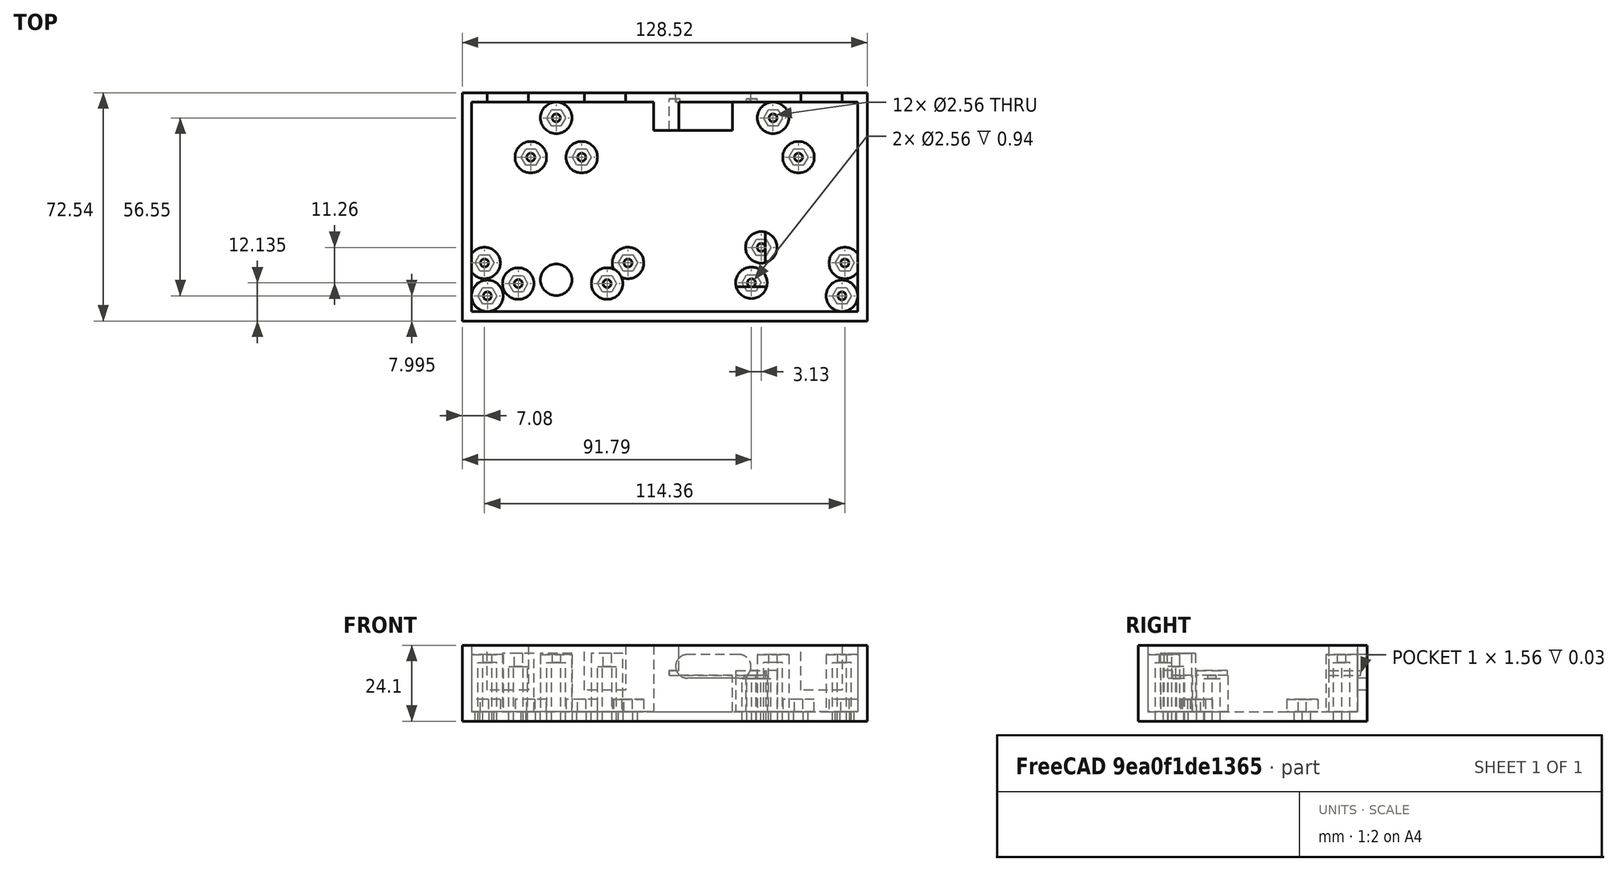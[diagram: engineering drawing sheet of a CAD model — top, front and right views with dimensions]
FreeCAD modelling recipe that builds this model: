
FCSTD DOCUMENT  (FreeCAD 1.0R38641 +678 (Git))
Label: box
License: All rights reserved
LicenseURL: https://en.wikipedia.org/wiki/All_rights_reserved
objects: Sketcher::SketchObject×19, PartDesign::Pocket×11, PartDesign::Pad×7, PartDesign::CoordinateSystem×1, PartDesign::Body×1
note: 94 computed .brp shape members not serialized (recipe doc carries the construction recipe); baked Part::Feature solids carry a one-line shape summary decoded from their .brp

FEATURE [Sketcher::SketchObject] Sketch
  ArcFitTolerance = 1e-06
  AttachmentSupport = -> [XY_Plane]
  FullyConstrained = true
  MakeInternals = false
  MapMode = 5
  sketch-geometry (4):
    g0: LineSegment StartX=-64.26 StartY=-36.275 StartZ=0 EndX=64.26 EndY=-36.275 EndZ=0
    g1: LineSegment StartX=64.26 StartY=-36.275 StartZ=0 EndX=64.26 EndY=36.275 EndZ=0
    g2: LineSegment StartX=64.26 StartY=36.275 StartZ=0 EndX=-64.26 EndY=36.275 EndZ=0
    g3: LineSegment StartX=-64.26 StartY=36.275 StartZ=0 EndX=-64.26 EndY=-36.275 EndZ=0
  constraints (12):
    c: Coincident(g0,g1)
    c: Coincident(g1,g2)
    c: Coincident(g2,g3)
    c: Coincident(g3,g0)
    c: Horizontal(g0)
    c: Horizontal(g2)
    c: Vertical(g1)
    c: Vertical(g3)
    c: DistanceX(g2,g2) = 128.52
    c: DistanceX(g-1,g1) = 64.26
    c: DistanceY(g3,g3) = 72.55
    c: DistanceY(g0,g-1) = 36.275
FEATURE [PartDesign::Pad] Pad
  Direction = (0,0,1)
  Length = 24.1
  Length2 = 10
  Profile = -> Sketch
  ReferenceAxis = -> Sketch [N_Axis]
  Refine = true
  Suppressed = false
  Type = 0
FEATURE [Sketcher::SketchObject] Sketch001
  ArcFitTolerance = 1e-06
  AttachmentSupport = -> [Pad]
  ExternalGeometry = -> [Pad]
  FullyConstrained = true
  MakeInternals = false
  MapMode = 5
  Placement = pos=(0,0,24.1) rot=(0,0,1;0rad)
  sketch-geometry (4):
    g0: LineSegment StartX=-61.26 StartY=-33.275 StartZ=0 EndX=61.26 EndY=-33.275 EndZ=0
    g1: LineSegment StartX=61.26 StartY=-33.275 StartZ=0 EndX=61.26 EndY=33.275 EndZ=0
    g2: LineSegment StartX=61.26 StartY=33.275 StartZ=0 EndX=-61.26 EndY=33.275 EndZ=0
    g3: LineSegment StartX=-61.26 StartY=33.275 StartZ=0 EndX=-61.26 EndY=-33.275 EndZ=0
  constraints (12):
    c: Coincident(g0,g1)
    c: Coincident(g1,g2)
    c: Coincident(g2,g3)
    c: Coincident(g3,g0)
    c: Horizontal(g0)
    c: Horizontal(g2)
    c: Vertical(g1)
    c: Vertical(g3)
    c: DistanceX(g-3,g2) = 3
    c: DistanceX(g0,g-4) = 3
    c: DistanceY(g-3,g0) = 3
    c: DistanceY(g1,g-4) = 3
FEATURE [PartDesign::Pocket] Pocket
  BaseFeature = -> Pad
  Direction = (0,0,-1)
  Length = 21.1
  Length2 = 5
  Profile = -> Sketch001
  ReferenceAxis = -> Sketch001 [N_Axis]
  Refine = true
  Suppressed = false
  Type = 0
FEATURE [Sketcher::SketchObject] Sketch002
  ArcFitTolerance = 1e-06
  AttachmentSupport = -> [Pocket]
  ExternalGeometry = -> [Pocket]
  FullyConstrained = true
  MakeInternals = false
  MapMode = 5
  Placement = pos=(0,0,3) rot=(0,0,1;0rad)
  sketch-geometry (6):
    g0: Circle CenterX=-42.48 CenterY=15.775 CenterZ=0 NormalX=0 NormalY=0 NormalZ=1 AngleXU=0 Radius=5
    g1: Circle CenterX=-57.18 CenterY=-17.825 CenterZ=0 NormalX=0 NormalY=0 NormalZ=1 AngleXU=0 Radius=5
    g2: Circle CenterX=-26.32 CenterY=15.775 CenterZ=0 NormalX=0 NormalY=0 NormalZ=1 AngleXU=0 Radius=5
    g3: Circle CenterX=-11.62 CenterY=-17.825 CenterZ=0 NormalX=0 NormalY=0 NormalZ=1 AngleXU=0 Radius=5
    g4: Circle CenterX=42.48 CenterY=15.775 CenterZ=0 NormalX=0 NormalY=0 NormalZ=1 AngleXU=0 Radius=5
    g5: Circle CenterX=57.18 CenterY=-17.825 CenterZ=0 NormalX=0 NormalY=0 NormalZ=1 AngleXU=0 Radius=5
  constraints (18):
    c: Radius(g0) = 5
    c: Equal(g0,g2)
    c: Equal(g2,g4)
    c: Equal(g4,g5)
    c: Equal(g5,g3)
    c: Equal(g3,g1)
    c: DistanceX(g-3,g0) = 21.78
    c: DistanceX(g-3,g2) = 37.94
    c: DistanceX(g4,g-4) = 21.78
    c: DistanceX(g5,g-4) = 7.08
    c: DistanceX(g-3,g1) = 7.08
    c: DistanceX(g-3,g3) = 52.64
    c: DistanceY(g0,g-3) = 20.5
    c: DistanceY(g-3,g1) = 18.45
    c: DistanceY(g0,g2) = 0
    c: DistanceY(g2,g4) = 0
    c: DistanceY(g1,g3) = 0
    c: DistanceY(g3,g5) = 0
FEATURE [PartDesign::Pad] Pad001
  BaseFeature = -> Pocket
  Direction = (0,0,1)
  Length = 3.9
  Length2 = 10
  Profile = -> Sketch002
  ReferenceAxis = -> Sketch002 [N_Axis]
  Refine = true
  Suppressed = false
  Type = 0
FEATURE [Sketcher::SketchObject] Sketch003
  ArcFitTolerance = 1e-06
  AttachmentSupport = -> [Pad001]
  ExternalGeometry = -> [Pad001]
  FullyConstrained = true
  MakeInternals = false
  MapMode = 5
  Placement = pos=(0,0,6.9) rot=(0,0,1;0rad)
  sketch-geometry (6):
    g0: Circle CenterX=-42.48 CenterY=15.775 CenterZ=0 NormalX=0 NormalY=0 NormalZ=1 AngleXU=0 Radius=1.28
    g1: Circle CenterX=-26.32 CenterY=15.775 CenterZ=0 NormalX=0 NormalY=0 NormalZ=1 AngleXU=0 Radius=1.28
    g2: Circle CenterX=42.48 CenterY=15.775 CenterZ=0 NormalX=0 NormalY=0 NormalZ=1 AngleXU=0 Radius=1.28
    g3: Circle CenterX=57.18 CenterY=-17.825 CenterZ=0 NormalX=0 NormalY=0 NormalZ=1 AngleXU=0 Radius=1.28
    g4: Circle CenterX=-11.62 CenterY=-17.825 CenterZ=0 NormalX=0 NormalY=0 NormalZ=1 AngleXU=0 Radius=1.28
    g5: Circle CenterX=-57.18 CenterY=-17.825 CenterZ=0 NormalX=0 NormalY=0 NormalZ=1 AngleXU=0 Radius=1.28
  constraints (12):
    c: Radius(g0) = 1.28
    c: Equal(g0,g1)
    c: Equal(g1,g2)
    c: Equal(g2,g3)
    c: Equal(g3,g4)
    c: Equal(g4,g5)
    c: Coincident(g0,g-3)
    c: Coincident(g1,g-4)
    c: Coincident(g2,g-5)
    c: Coincident(g3,g-6)
    c: Coincident(g4,g-7)
    c: Coincident(g5,g-8)
FEATURE [PartDesign::Pocket] Pocket001
  BaseFeature = -> Pad001
  Direction = (0,0,-1)
  Length = 3.9
  Length2 = 5
  Profile = -> Sketch003
  ReferenceAxis = -> Sketch003 [N_Axis]
  Refine = true
  Suppressed = false
  Type = 0
FEATURE [Sketcher::SketchObject] Sketch004
  ArcFitTolerance = 1e-06
  AttachmentSupport = -> [Pocket001]
  ExternalGeometry = -> [Pocket001]
  FullyConstrained = true
  MakeInternals = false
  MapMode = 5
  Placement = pos=(0,0,3) rot=(0,0,1;0rad)
  sketch-geometry (6):
    g0: LineSegment StartX=-3.54 StartY=24.275 StartZ=0 EndX=21.46 EndY=24.275 EndZ=0
    g1: LineSegment StartX=21.46 StartY=24.275 StartZ=0 EndX=21.46 EndY=34.275 EndZ=0
    g2: LineSegment StartX=21.46 StartY=34.275 StartZ=0 EndX=-3.54 EndY=34.275 EndZ=0
    g3: LineSegment StartX=-3.54 StartY=34.275 StartZ=0 EndX=-3.54 EndY=24.275 EndZ=0
    g4: Circle CenterX=27.53 CenterY=-24.135 CenterZ=0 NormalX=0 NormalY=0 NormalZ=1 AngleXU=0 Radius=5
    g5: Circle CenterX=30.66 CenterY=-12.875 CenterZ=0 NormalX=0 NormalY=0 NormalZ=1 AngleXU=0 Radius=5
  constraints (18):
    c: Coincident(g0,g1)
    c: Coincident(g1,g2)
    c: Coincident(g2,g3)
    c: Coincident(g3,g0)
    c: Horizontal(g0)
    c: Horizontal(g2)
    c: Vertical(g1)
    c: Vertical(g3)
    c: Radius(g5) = 5
    c: Equal(g5,g4)
    c: DistanceY(g3,g3) = 10
    c: DistanceX(g0,g0) = 25
    c: DistanceX(g1,g-3) = 42.8
    c: DistanceY(g1,g-3) = 2
    c: DistanceY(g-3,g5) = 23.4
    c: DistanceY(g-3,g4) = 12.14
    c: DistanceX(g5,g-3) = 33.6
    c: DistanceX(g4,g-3) = 36.73
FEATURE [PartDesign::Pad] Pad002
  BaseFeature = -> Pocket001
  Direction = (0,0,1)
  Length = 11.5
  Length2 = 10
  Profile = -> Sketch004
  ReferenceAxis = -> Sketch004 [N_Axis]
  Refine = true
  Suppressed = false
  Type = 0
FEATURE [Sketcher::SketchObject] Sketch005
  ArcFitTolerance = 1e-06
  AttachmentSupport = -> [Pad002]
  ExternalGeometry = -> [Pad002]
  FullyConstrained = true
  MakeInternals = false
  MapMode = 5
  Placement = pos=(0,0,14.5) rot=(0,0,1;0rad)
  sketch-geometry (2):
    g0: Circle CenterX=30.66 CenterY=-12.875 CenterZ=0 NormalX=0 NormalY=0 NormalZ=1 AngleXU=0 Radius=1.28
    g1: Circle CenterX=27.53 CenterY=-24.135 CenterZ=0 NormalX=0 NormalY=0 NormalZ=1 AngleXU=0 Radius=1.28
  constraints (4):
    c: Radius(g0) = 1.28
    c: Equal(g0,g1)
    c: Coincident(g0,g-3)
    c: Coincident(g1,g-4)
FEATURE [PartDesign::Pocket] Pocket002
  BaseFeature = -> Pad002
  Direction = (0,0,-1)
  Length = 3.94
  Length2 = 5
  Profile = -> Sketch005
  ReferenceAxis = -> Sketch005 [N_Axis]
  Refine = true
  Suppressed = false
  Type = 0
FEATURE [Sketcher::SketchObject] Sketch006
  ArcFitTolerance = 1e-06
  AttachmentSupport = -> [Pocket002]
  ExternalGeometry = -> [Pocket002]
  FullyConstrained = true
  MakeInternals = false
  MapMode = 5
  Placement = pos=(0,0,3) rot=(0,0,1;0rad)
  sketch-geometry (3):
    g0: Circle CenterX=-46.46 CenterY=-24.375 CenterZ=0 NormalX=0 NormalY=0 NormalZ=1 AngleXU=0 Radius=5
    g1: Circle CenterX=-18.26 CenterY=-24.375 CenterZ=0 NormalX=0 NormalY=0 NormalZ=1 AngleXU=0 Radius=5
    g2: Circle CenterX=-34.4 CenterY=-23.175 CenterZ=0 NormalX=0 NormalY=0 NormalZ=1 AngleXU=0 Radius=5
  constraints (9):
    c: Radius(g0) = 5
    c: Equal(g0,g2)
    c: Equal(g2,g1)
    c: DistanceX(g-3,g0) = 17.8
    c: DistanceX(g-3,g2) = 29.86
    c: DistanceX(g-3,g1) = 46
    c: DistanceY(g-3,g0) = 11.9
    c: DistanceY(g0,g1) = 0
    c: DistanceY(g-3,g2) = 13.1
FEATURE [PartDesign::Pad] Pad003
  BaseFeature = -> Pocket002
  Direction = (0,0,1)
  Length = 18.5
  Length2 = 10
  Profile = -> Sketch006
  ReferenceAxis = -> Sketch006 [N_Axis]
  Refine = true
  Suppressed = false
  Type = 0
FEATURE [Sketcher::SketchObject] Sketch007
  ArcFitTolerance = 1e-06
  AttachmentSupport = -> [Pad003]
  ExternalGeometry = -> [Pad003]
  FullyConstrained = true
  MakeInternals = false
  MapMode = 5
  Placement = pos=(0,0,21.5) rot=(0,0,1;0rad)
  sketch-geometry (2):
    g0: Circle CenterX=-46.46 CenterY=-24.375 CenterZ=0 NormalX=0 NormalY=0 NormalZ=1 AngleXU=0 Radius=1.28
    g1: Circle CenterX=-18.26 CenterY=-24.375 CenterZ=0 NormalX=0 NormalY=0 NormalZ=1 AngleXU=0 Radius=1.28
  constraints (4):
    c: Radius(g0) = 1.28
    c: Radius(g1) = 1.28
    c: Coincident(g0,g-4)
    c: Coincident(g1,g-3)
FEATURE [PartDesign::Pocket] Pocket003
  BaseFeature = -> Pad003
  Direction = (0,0,-1)
  Length = 4.1
  Length2 = 5
  Profile = -> Sketch007
  ReferenceAxis = -> Sketch007 [N_Axis]
  Refine = true
  Suppressed = false
  Type = 0
FEATURE [Sketcher::SketchObject] Sketch008
  ArcFitTolerance = 1e-06
  AttachmentSupport = -> [Pocket003]
  ExternalGeometry = -> [Pocket003]
  FullyConstrained = true
  MakeInternals = false
  MapMode = 5
  Placement = pos=(0,0,3) rot=(0,0,1;0rad)
  sketch-geometry (4):
    g0: Circle CenterX=-34.4 CenterY=28.275 CenterZ=0 NormalX=0 NormalY=0 NormalZ=1 AngleXU=0 Radius=5
    g1: Circle CenterX=34.4 CenterY=28.275 CenterZ=0 NormalX=0 NormalY=0 NormalZ=1 AngleXU=0 Radius=5
    g2: Circle CenterX=-56.26 CenterY=-28.275 CenterZ=0 NormalX=0 NormalY=0 NormalZ=1 AngleXU=0 Radius=5
    g3: Circle CenterX=56.26 CenterY=-28.275 CenterZ=0 NormalX=0 NormalY=0 NormalZ=1 AngleXU=0 Radius=5
  constraints (12):
    c: Radius(g0) = 5
    c: Equal(g1,g0)
    c: Equal(g1,g2)
    c: Equal(g2,g3)
    c: DistanceX(g-3,g0) = 29.86
    c: DistanceX(g1,g-4) = 29.86
    c: DistanceX(g-3,g2) = 8
    c: DistanceX(g3,g-4) = 8
    c: DistanceY(g0,g-3) = 8
    c: DistanceY(g1,g-4) = 8
    c: DistanceY(g-4,g3) = 8
    c: DistanceY(g-3,g2) = 8
FEATURE [PartDesign::Pad] Pad004
  BaseFeature = -> Pocket003
  Direction = (0,0,1)
  Length = 18.1
  Length2 = 10
  Profile = -> Sketch008
  ReferenceAxis = -> Sketch008 [N_Axis]
  Refine = true
  Suppressed = false
  Type = 0
FEATURE [Sketcher::SketchObject] Sketch009
  ArcFitTolerance = 1e-06
  AttachmentSupport = -> [Pad004]
  ExternalGeometry = -> [Pad004]
  FullyConstrained = true
  MakeInternals = false
  MapMode = 5
  Placement = pos=(0,0,21.1) rot=(0,0,1;0rad)
  sketch-geometry (4):
    g0: Circle CenterX=-34.4 CenterY=28.275 CenterZ=0 NormalX=0 NormalY=0 NormalZ=1 AngleXU=0 Radius=1.28
    g1: Circle CenterX=34.4 CenterY=28.275 CenterZ=0 NormalX=0 NormalY=0 NormalZ=1 AngleXU=0 Radius=1.28
    g2: Circle CenterX=56.26 CenterY=-28.275 CenterZ=0 NormalX=0 NormalY=0 NormalZ=1 AngleXU=0 Radius=1.28
    g3: Circle CenterX=-56.26 CenterY=-28.275 CenterZ=0 NormalX=0 NormalY=0 NormalZ=1 AngleXU=0 Radius=1.28
  constraints (8):
    c: Radius(g0) = 1.28
    c: Equal(g0,g1)
    c: Equal(g1,g2)
    c: Equal(g2,g3)
    c: Coincident(g0,g-3)
    c: Coincident(g1,g-4)
    c: Coincident(g2,g-5)
    c: Coincident(g3,g-6)
FEATURE [PartDesign::Pocket] Pocket004
  BaseFeature = -> Pad004
  Direction = (0,0,-1)
  Length = 2.5
  Length2 = 5
  Profile = -> Sketch009
  ReferenceAxis = -> Sketch009 [N_Axis]
  Refine = true
  Suppressed = false
  Type = 0
FEATURE [Sketcher::SketchObject] Sketch010
  ArcFitTolerance = 1e-06
  AttachmentSupport = -> [Pocket004]
  ExternalGeometry = -> [Pocket004]
  FullyConstrained = true
  MakeInternals = false
  MapMode = 5
  Placement = pos=(0,0,0) rot=(1,0,0;3.14159rad)
  sketch-geometry (42):
    g0: LineSegment StartX=-54.18 StartY=17.825 StartZ=0 EndX=-55.68 EndY=20.4231 EndZ=0
    g1: LineSegment StartX=-55.68 StartY=20.4231 StartZ=0 EndX=-58.68 EndY=20.4231 EndZ=0
    g2: LineSegment StartX=-58.68 StartY=20.4231 StartZ=0 EndX=-60.18 EndY=17.825 EndZ=0
    g3: LineSegment StartX=-60.18 StartY=17.825 StartZ=0 EndX=-58.68 EndY=15.2269 EndZ=0
    g4: LineSegment StartX=-58.68 StartY=15.2269 StartZ=0 EndX=-55.68 EndY=15.2269 EndZ=0
    g5: LineSegment StartX=-55.68 StartY=15.2269 StartZ=0 EndX=-54.18 EndY=17.825 EndZ=0
    g6: Circle [constr] CenterX=-57.18 CenterY=17.825 CenterZ=0 NormalX=0 NormalY=0 NormalZ=1 AngleXU=0 Radius=3
    g7: LineSegment StartX=-40.98 StartY=-18.3731 StartZ=0 EndX=-39.48 EndY=-15.775 EndZ=0
    g8: LineSegment StartX=-39.48 StartY=-15.775 StartZ=0 EndX=-40.98 EndY=-13.1769 EndZ=0
    g9: LineSegment StartX=-40.98 StartY=-13.1769 StartZ=0 EndX=-43.98 EndY=-13.1769 EndZ=0
    g10: LineSegment StartX=-43.98 StartY=-13.1769 StartZ=0 EndX=-45.48 EndY=-15.775 EndZ=0
    g11: LineSegment StartX=-45.48 StartY=-15.775 StartZ=0 EndX=-43.98 EndY=-18.3731 EndZ=0
    g12: LineSegment StartX=-43.98 StartY=-18.3731 StartZ=0 EndX=-40.98 EndY=-18.3731 EndZ=0
    g13: Circle [constr] CenterX=-42.48 CenterY=-15.775 CenterZ=0 NormalX=0 NormalY=0 NormalZ=1 AngleXU=0 Radius=3
    g14: LineSegment StartX=-23.32 StartY=-15.775 StartZ=0 EndX=-24.82 EndY=-13.1769 EndZ=0
    g15: LineSegment StartX=-24.82 StartY=-13.1769 StartZ=0 EndX=-27.82 EndY=-13.1769 EndZ=0
    g16: LineSegment StartX=-27.82 StartY=-13.1769 StartZ=0 EndX=-29.32 EndY=-15.775 EndZ=0
    g17: LineSegment StartX=-29.32 StartY=-15.775 StartZ=0 EndX=-27.82 EndY=-18.3731 EndZ=0
    g18: LineSegment StartX=-27.82 StartY=-18.3731 StartZ=0 EndX=-24.82 EndY=-18.3731 EndZ=0
    g19: LineSegment StartX=-24.82 StartY=-18.3731 StartZ=0 EndX=-23.32 EndY=-15.775 EndZ=0
    g20: Circle [constr] CenterX=-26.32 CenterY=-15.775 CenterZ=0 NormalX=0 NormalY=0 NormalZ=1 AngleXU=0 Radius=3
    g21: LineSegment StartX=-10.12 StartY=15.2269 StartZ=0 EndX=-8.62 EndY=17.825 EndZ=0
    g22: LineSegment StartX=-8.62 StartY=17.825 StartZ=0 EndX=-10.12 EndY=20.4231 EndZ=0
    g23: LineSegment StartX=-10.12 StartY=20.4231 StartZ=0 EndX=-13.12 EndY=20.4231 EndZ=0
    g24: LineSegment StartX=-13.12 StartY=20.4231 StartZ=0 EndX=-14.62 EndY=17.825 EndZ=0
    g25: LineSegment StartX=-14.62 StartY=17.825 StartZ=0 EndX=-13.12 EndY=15.2269 EndZ=0
    g26: LineSegment StartX=-13.12 StartY=15.2269 StartZ=0 EndX=-10.12 EndY=15.2269 EndZ=0
    g27: Circle [constr] CenterX=-11.62 CenterY=17.825 CenterZ=0 NormalX=0 NormalY=0 NormalZ=1 AngleXU=0 Radius=3
    g28: LineSegment StartX=58.68 StartY=15.2269 StartZ=0 EndX=60.18 EndY=17.825 EndZ=0
    g29: LineSegment StartX=60.18 StartY=17.825 StartZ=0 EndX=58.68 EndY=20.4231 EndZ=0
    g30: LineSegment StartX=58.68 StartY=20.4231 StartZ=0 EndX=55.68 EndY=20.4231 EndZ=0
    g31: LineSegment StartX=55.68 StartY=20.4231 StartZ=0 EndX=54.18 EndY=17.825 EndZ=0
    g32: LineSegment StartX=54.18 StartY=17.825 StartZ=0 EndX=55.68 EndY=15.2269 EndZ=0
    g33: LineSegment StartX=55.68 StartY=15.2269 StartZ=0 EndX=58.68 EndY=15.2269 EndZ=0
    g34: Circle [constr] CenterX=57.18 CenterY=17.825 CenterZ=0 NormalX=0 NormalY=0 NormalZ=1 AngleXU=0 Radius=3
    g35: LineSegment StartX=43.98 StartY=-18.3731 StartZ=0 EndX=45.48 EndY=-15.775 EndZ=0
    g36: LineSegment StartX=45.48 StartY=-15.775 StartZ=0 EndX=43.98 EndY=-13.1769 EndZ=0
    g37: LineSegment StartX=43.98 StartY=-13.1769 StartZ=0 EndX=40.98 EndY=-13.1769 EndZ=0
    g38: LineSegment StartX=40.98 StartY=-13.1769 StartZ=0 EndX=39.48 EndY=-15.775 EndZ=0
    g39: LineSegment StartX=39.48 StartY=-15.775 StartZ=0 EndX=40.98 EndY=-18.3731 EndZ=0
    g40: LineSegment StartX=40.98 StartY=-18.3731 StartZ=0 EndX=43.98 EndY=-18.3731 EndZ=0
    g41: Circle [constr] CenterX=42.48 CenterY=-15.775 CenterZ=0 NormalX=0 NormalY=0 NormalZ=1 AngleXU=0 Radius=3
  constraints (102):
    c: Coincident(g0,g1)
    c: Coincident(g1,g2)
    c: Coincident(g2,g3)
    c: Coincident(g3,g4)
    c: Coincident(g4,g5)
    c: Coincident(g5,g0)
    c: Equal(g0, g1-g5) x5
    c: PointOnObject(g0,g6)
    c: PointOnObject(g1,g6)
    c: PointOnObject(g2,g6)
    c: PointOnObject(g3,g6)
    c: PointOnObject(g4,g6)
    c: PointOnObject(g5,g6)
    c: Coincident(g7,g8)
    c: Coincident(g8,g9)
    c: Coincident(g9,g10)
    c: Coincident(g10,g11)
    c: Coincident(g11,g12)
    c: Coincident(g12,g7)
    c: Equal(g7, g8-g12) x5
    c: PointOnObject(g7,g13)
    c: PointOnObject(g8,g13)
    c: PointOnObject(g9,g13)
    c: PointOnObject(g10,g13)
    c: PointOnObject(g11,g13)
    c: PointOnObject(g12,g13)
    c: Coincident(g14,g15)
    c: Coincident(g15,g16)
    c: Coincident(g16,g17)
    c: Coincident(g17,g18)
    c: Coincident(g18,g19)
    c: Coincident(g19,g14)
    c: Equal(g14, g15-g19) x5
    c: PointOnObject(g14,g20)
    c: PointOnObject(g15,g20)
    c: PointOnObject(g16,g20)
    c: PointOnObject(g17,g20)
    c: PointOnObject(g18,g20)
    c: PointOnObject(g19,g20)
    c: Coincident(g21,g22)
    c: Coincident(g22,g23)
    c: Coincident(g23,g24)
    c: Coincident(g24,g25)
    c: Coincident(g25,g26)
    c: Coincident(g26,g21)
    c: Equal(g21, g22-g26) x5
    c: PointOnObject(g21,g27)
    c: PointOnObject(g22,g27)
    c: PointOnObject(g23,g27)
    c: PointOnObject(g24,g27)
    c: PointOnObject(g25,g27)
    c: PointOnObject(g26,g27)
    c: Coincident(g28,g29)
    c: Coincident(g29,g30)
    c: Coincident(g30,g31)
    c: Coincident(g31,g32)
    c: Coincident(g32,g33)
    c: Coincident(g33,g28)
    c: Equal(g28, g29-g33) x5
    c: PointOnObject(g28,g34)
    c: PointOnObject(g29,g34)
    c: PointOnObject(g30,g34)
    c: PointOnObject(g31,g34)
    c: PointOnObject(g32,g34)
    c: PointOnObject(g33,g34)
    c: Coincident(g35,g36)
    c: Coincident(g36,g37)
    c: Coincident(g37,g38)
    c: Coincident(g38,g39)
    c: Coincident(g39,g40)
    c: Coincident(g40,g35)
    c: Equal(g35, g36-g40) x5
    c: PointOnObject(g35,g41)
    c: PointOnObject(g36,g41)
    c: PointOnObject(g37,g41)
    c: PointOnObject(g38,g41)
    c: PointOnObject(g39,g41)
    c: PointOnObject(g40,g41)
    c: Radius(g6) = 3
    c: Horizontal(g1)
    c: Horizontal(g23)
    c: Horizontal(g30)
    c: Horizontal(g37)
    c: Horizontal(g15)
    c: Horizontal(g9)
    c: Equal(g6,g27)
    c: Equal(g27,g34)
    c: Equal(g34,g41)
    c: Equal(g41,g20)
    c: Equal(g20,g13)
    c: DistanceY(g6,g27) = 0
    c: DistanceY(g27,g34) = 0
    c: DistanceY(g41,g20) = 0
    c: DistanceY(g13,g20) = 0
    c: DistanceX(g-3,g6) = 7.08
    c: DistanceX(g34,g-4) = 7.08
    c: DistanceX(g-3,g13) = 21.78
    c: DistanceX(g41,g-4) = 21.78
    c: DistanceX(g-3,g20) = 37.94
    c: DistanceY(g-3,g13) = 20.5
    c: DistanceY(g6,g-3) = 18.45
    c: DistanceX(g-3,g27) = 52.64
FEATURE [PartDesign::Pocket] Pocket005
  BaseFeature = -> Pocket004
  Direction = (0,0,1)
  Length = 3
  Length2 = 5
  Profile = -> Sketch010
  ReferenceAxis = -> Sketch010 [N_Axis]
  Refine = true
  Suppressed = false
  Type = 0
FEATURE [Sketcher::SketchObject] Sketch011
  ArcFitTolerance = 1e-06
  AttachmentSupport = -> [Pocket005]
  ExternalGeometry = -> [Pocket005]
  FullyConstrained = true
  MakeInternals = false
  MapMode = 5
  Placement = pos=(0,0,0) rot=(1,0,0;3.14159rad)
  sketch-geometry (14):
    g0: LineSegment StartX=30.53 StartY=24.135 StartZ=0 EndX=29.03 EndY=26.7331 EndZ=0
    g1: LineSegment StartX=29.03 StartY=26.7331 StartZ=0 EndX=26.03 EndY=26.7331 EndZ=0
    g2: LineSegment StartX=26.03 StartY=26.7331 StartZ=0 EndX=24.53 EndY=24.135 EndZ=0
    g3: LineSegment StartX=24.53 StartY=24.135 StartZ=0 EndX=26.03 EndY=21.5369 EndZ=0
    g4: LineSegment StartX=26.03 StartY=21.5369 StartZ=0 EndX=29.03 EndY=21.5369 EndZ=0
    g5: LineSegment StartX=29.03 StartY=21.5369 StartZ=0 EndX=30.53 EndY=24.135 EndZ=0
    g6: Circle [constr] CenterX=27.53 CenterY=24.135 CenterZ=0 NormalX=0 NormalY=0 NormalZ=1 AngleXU=0 Radius=3
    g7: LineSegment StartX=32.16 StartY=10.2769 StartZ=0 EndX=33.66 EndY=12.875 EndZ=0
    g8: LineSegment StartX=33.66 StartY=12.875 StartZ=0 EndX=32.16 EndY=15.4731 EndZ=0
    g9: LineSegment StartX=32.16 StartY=15.4731 StartZ=0 EndX=29.16 EndY=15.4731 EndZ=0
    g10: LineSegment StartX=29.16 StartY=15.4731 StartZ=0 EndX=27.66 EndY=12.875 EndZ=0
    g11: LineSegment StartX=27.66 StartY=12.875 StartZ=0 EndX=29.16 EndY=10.2769 EndZ=0
    g12: LineSegment StartX=29.16 StartY=10.2769 StartZ=0 EndX=32.16 EndY=10.2769 EndZ=0
    g13: Circle [constr] CenterX=30.66 CenterY=12.875 CenterZ=0 NormalX=0 NormalY=0 NormalZ=1 AngleXU=0 Radius=3
  constraints (34):
    c: Coincident(g0,g1)
    c: Coincident(g1,g2)
    c: Coincident(g2,g3)
    c: Coincident(g3,g4)
    c: Coincident(g4,g5)
    c: Coincident(g5,g0)
    c: Equal(g0, g1-g5) x5
    c: PointOnObject(g0,g6)
    c: PointOnObject(g1,g6)
    c: PointOnObject(g2,g6)
    c: PointOnObject(g3,g6)
    c: PointOnObject(g4,g6)
    c: PointOnObject(g5,g6)
    c: Coincident(g7,g8)
    c: Coincident(g8,g9)
    c: Coincident(g9,g10)
    c: Coincident(g10,g11)
    c: Coincident(g11,g12)
    c: Coincident(g12,g7)
    c: Equal(g7, g8-g12) x5
    c: PointOnObject(g7,g13)
    c: PointOnObject(g8,g13)
    c: PointOnObject(g9,g13)
    c: PointOnObject(g10,g13)
    c: PointOnObject(g11,g13)
    c: PointOnObject(g12,g13)
    c: Horizontal(g1)
    c: Horizontal(g9)
    c: Radius(g6) = 3
    c: Equal(g6,g13)
    c: DistanceX(g6,g-3) = 36.73
    c: DistanceY(g6,g-3) = 12.14
    c: DistanceX(g13,g-3) = 33.6
    c: DistanceY(g13,g-3) = 23.4
FEATURE [PartDesign::Pocket] Pocket006
  BaseFeature = -> Pocket005
  Direction = (0,0,1)
  Length = 13.56
  Length2 = 5
  Profile = -> Sketch011
  ReferenceAxis = -> Sketch011 [N_Axis]
  Refine = true
  Suppressed = false
  Type = 0
FEATURE [Sketcher::SketchObject] Sketch012
  ArcFitTolerance = 1e-06
  AttachmentSupport = -> [Pocket006]
  ExternalGeometry = -> [Pocket006]
  FullyConstrained = true
  MakeInternals = false
  MapMode = 5
  Placement = pos=(0,0,0) rot=(1,0,0;3.14159rad)
  sketch-geometry (14):
    g0: LineSegment StartX=-43.46 StartY=24.375 StartZ=0 EndX=-44.96 EndY=26.9731 EndZ=0
    g1: LineSegment StartX=-44.96 StartY=26.9731 StartZ=0 EndX=-47.96 EndY=26.9731 EndZ=0
    g2: LineSegment StartX=-47.96 StartY=26.9731 StartZ=0 EndX=-49.46 EndY=24.375 EndZ=0
    g3: LineSegment StartX=-49.46 StartY=24.375 StartZ=0 EndX=-47.96 EndY=21.7769 EndZ=0
    g4: LineSegment StartX=-47.96 StartY=21.7769 StartZ=0 EndX=-44.96 EndY=21.7769 EndZ=0
    g5: LineSegment StartX=-44.96 StartY=21.7769 StartZ=0 EndX=-43.46 EndY=24.375 EndZ=0
    g6: Circle [constr] CenterX=-46.46 CenterY=24.375 CenterZ=0 NormalX=0 NormalY=0 NormalZ=1 AngleXU=0 Radius=3
    g7: LineSegment StartX=-15.26 StartY=24.375 StartZ=0 EndX=-16.76 EndY=26.9731 EndZ=0
    g8: LineSegment StartX=-16.76 StartY=26.9731 StartZ=0 EndX=-19.76 EndY=26.9731 EndZ=0
    g9: LineSegment StartX=-19.76 StartY=26.9731 StartZ=0 EndX=-21.26 EndY=24.375 EndZ=0
    g10: LineSegment StartX=-21.26 StartY=24.375 StartZ=0 EndX=-19.76 EndY=21.7769 EndZ=0
    g11: LineSegment StartX=-19.76 StartY=21.7769 StartZ=0 EndX=-16.76 EndY=21.7769 EndZ=0
    g12: LineSegment StartX=-16.76 StartY=21.7769 StartZ=0 EndX=-15.26 EndY=24.375 EndZ=0
    g13: Circle [constr] CenterX=-18.26 CenterY=24.375 CenterZ=0 NormalX=0 NormalY=0 NormalZ=1 AngleXU=0 Radius=3
  constraints (34):
    c: Coincident(g0,g1)
    c: Coincident(g1,g2)
    c: Coincident(g2,g3)
    c: Coincident(g3,g4)
    c: Coincident(g4,g5)
    c: Coincident(g5,g0)
    c: Equal(g0, g1-g5) x5
    c: PointOnObject(g0,g6)
    c: PointOnObject(g1,g6)
    c: PointOnObject(g2,g6)
    c: PointOnObject(g3,g6)
    c: PointOnObject(g4,g6)
    c: PointOnObject(g5,g6)
    c: Coincident(g7,g8)
    c: Coincident(g8,g9)
    c: Coincident(g9,g10)
    c: Coincident(g10,g11)
    c: Coincident(g11,g12)
    c: Coincident(g12,g7)
    c: Equal(g7, g8-g12) x5
    c: PointOnObject(g7,g13)
    c: PointOnObject(g8,g13)
    c: PointOnObject(g9,g13)
    c: PointOnObject(g10,g13)
    c: PointOnObject(g11,g13)
    c: PointOnObject(g12,g13)
    c: Horizontal(g8)
    c: Horizontal(g1)
    c: Radius(g6) = 3
    c: Equal(g6,g13)
    c: DistanceX(g-3,g6) = 17.8
    c: DistanceY(g6,g-3) = 11.9
    c: DistanceY(g6,g13) = 0
    c: DistanceX(g-3,g13) = 46
FEATURE [PartDesign::Pocket] Pocket007
  BaseFeature = -> Pocket006
  Direction = (0,0,1)
  Length = 17.4
  Length2 = 5
  Profile = -> Sketch012
  ReferenceAxis = -> Sketch012 [N_Axis]
  Refine = true
  Suppressed = false
  Type = 0
FEATURE [Sketcher::SketchObject] Sketch013
  ArcFitTolerance = 1e-06
  AttachmentSupport = -> [Pocket007]
  ExternalGeometry = -> [Pocket007]
  FullyConstrained = true
  MakeInternals = false
  MapMode = 5
  Placement = pos=(0,0,0) rot=(1,0,0;3.14159rad)
  sketch-geometry (28):
    g0: LineSegment StartX=-54.76 StartY=25.6769 StartZ=0 EndX=-53.26 EndY=28.275 EndZ=0
    g1: LineSegment StartX=-53.26 StartY=28.275 StartZ=0 EndX=-54.76 EndY=30.8731 EndZ=0
    g2: LineSegment StartX=-54.76 StartY=30.8731 StartZ=0 EndX=-57.76 EndY=30.8731 EndZ=0
    g3: LineSegment StartX=-57.76 StartY=30.8731 StartZ=0 EndX=-59.26 EndY=28.275 EndZ=0
    g4: LineSegment StartX=-59.26 StartY=28.275 StartZ=0 EndX=-57.76 EndY=25.6769 EndZ=0
    g5: LineSegment StartX=-57.76 StartY=25.6769 StartZ=0 EndX=-54.76 EndY=25.6769 EndZ=0
    g6: Circle [constr] CenterX=-56.26 CenterY=28.275 CenterZ=0 NormalX=0 NormalY=0 NormalZ=1 AngleXU=0 Radius=3
    g7: LineSegment StartX=57.76 StartY=25.6769 StartZ=0 EndX=59.26 EndY=28.275 EndZ=0
    g8: LineSegment StartX=59.26 StartY=28.275 StartZ=0 EndX=57.76 EndY=30.8731 EndZ=0
    g9: LineSegment StartX=57.76 StartY=30.8731 StartZ=0 EndX=54.76 EndY=30.8731 EndZ=0
    g10: LineSegment StartX=54.76 StartY=30.8731 StartZ=0 EndX=53.26 EndY=28.275 EndZ=0
    g11: LineSegment StartX=53.26 StartY=28.275 StartZ=0 EndX=54.76 EndY=25.6769 EndZ=0
    g12: LineSegment StartX=54.76 StartY=25.6769 StartZ=0 EndX=57.76 EndY=25.6769 EndZ=0
    g13: Circle [constr] CenterX=56.26 CenterY=28.275 CenterZ=0 NormalX=0 NormalY=0 NormalZ=1 AngleXU=0 Radius=3
    g14: LineSegment StartX=32.9 StartY=-25.6769 StartZ=0 EndX=31.4 EndY=-28.275 EndZ=0
    g15: LineSegment StartX=31.4 StartY=-28.275 StartZ=0 EndX=32.9 EndY=-30.8731 EndZ=0
    g16: LineSegment StartX=32.9 StartY=-30.8731 StartZ=0 EndX=35.9 EndY=-30.8731 EndZ=0
    g17: LineSegment StartX=35.9 StartY=-30.8731 StartZ=0 EndX=37.4 EndY=-28.275 EndZ=0
    g18: LineSegment StartX=37.4 StartY=-28.275 StartZ=0 EndX=35.9 EndY=-25.6769 EndZ=0
    g19: LineSegment StartX=35.9 StartY=-25.6769 StartZ=0 EndX=32.9 EndY=-25.6769 EndZ=0
    g20: Circle [constr] CenterX=34.4 CenterY=-28.275 CenterZ=0 NormalX=0 NormalY=0 NormalZ=1 AngleXU=0 Radius=3
    g21: LineSegment StartX=-31.4 StartY=-28.275 StartZ=0 EndX=-32.9 EndY=-25.6769 EndZ=0
    g22: LineSegment StartX=-32.9 StartY=-25.6769 StartZ=0 EndX=-35.9 EndY=-25.6769 EndZ=0
    g23: LineSegment StartX=-35.9 StartY=-25.6769 StartZ=0 EndX=-37.4 EndY=-28.275 EndZ=0
    g24: LineSegment StartX=-37.4 StartY=-28.275 StartZ=0 EndX=-35.9 EndY=-30.8731 EndZ=0
    g25: LineSegment StartX=-35.9 StartY=-30.8731 StartZ=0 EndX=-32.9 EndY=-30.8731 EndZ=0
    g26: LineSegment StartX=-32.9 StartY=-30.8731 StartZ=0 EndX=-31.4 EndY=-28.275 EndZ=0
    g27: Circle [constr] CenterX=-34.4 CenterY=-28.275 CenterZ=0 NormalX=0 NormalY=0 NormalZ=1 AngleXU=0 Radius=3
  constraints (68):
    c: Coincident(g0,g1)
    c: Coincident(g1,g2)
    c: Coincident(g2,g3)
    c: Coincident(g3,g4)
    c: Coincident(g4,g5)
    c: Coincident(g5,g0)
    c: Equal(g0, g1-g5) x5
    c: PointOnObject(g0,g6)
    c: PointOnObject(g1,g6)
    c: PointOnObject(g2,g6)
    c: PointOnObject(g3,g6)
    c: PointOnObject(g4,g6)
    c: PointOnObject(g5,g6)
    c: Coincident(g7,g8)
    c: Coincident(g8,g9)
    c: Coincident(g9,g10)
    c: Coincident(g10,g11)
    c: Coincident(g11,g12)
    c: Coincident(g12,g7)
    c: Equal(g7, g8-g12) x5
    c: PointOnObject(g7,g13)
    c: PointOnObject(g8,g13)
    c: PointOnObject(g9,g13)
    c: PointOnObject(g10,g13)
    c: PointOnObject(g11,g13)
    c: PointOnObject(g12,g13)
    c: Coincident(g14,g15)
    c: Coincident(g15,g16)
    c: Coincident(g16,g17)
    c: Coincident(g17,g18)
    c: Coincident(g18,g19)
    c: Coincident(g19,g14)
    c: Equal(g14, g15-g19) x5
    c: PointOnObject(g14,g20)
    c: PointOnObject(g15,g20)
    c: PointOnObject(g16,g20)
    c: PointOnObject(g17,g20)
    c: PointOnObject(g18,g20)
    c: PointOnObject(g19,g20)
    c: Coincident(g21,g22)
    c: Coincident(g22,g23)
    c: Coincident(g23,g24)
    c: Coincident(g24,g25)
    c: Coincident(g25,g26)
    c: Coincident(g26,g21)
    c: Equal(g21, g22-g26) x5
    c: PointOnObject(g21,g27)
    c: PointOnObject(g22,g27)
    c: PointOnObject(g23,g27)
    c: PointOnObject(g24,g27)
    c: PointOnObject(g25,g27)
    c: PointOnObject(g26,g27)
    c: Horizontal(g2)
    c: Horizontal(g9)
    c: Horizontal(g22)
    c: Horizontal(g19)
    c: DistanceX(g-3,g6) = 8
    c: Radius(g6) = 3
    c: Equal(g6,g13)
    c: Equal(g13,g20)
    c: Equal(g20,g27)
    c: DistanceX(g-3,g27) = 29.86
    c: DistanceX(g20,g-4) = 29.86
    c: DistanceX(g13,g-4) = 8
    c: DistanceY(g6,g-3) = 8
    c: DistanceY(g13,g-4) = 8
    c: DistanceY(g-4,g20) = 8
    c: DistanceY(g-3,g27) = 8
FEATURE [PartDesign::Pocket] Pocket008
  BaseFeature = -> Pocket007
  Direction = (0,0,1)
  Length = 18.6
  Length2 = 5
  Profile = -> Sketch013
  ReferenceAxis = -> Sketch013 [N_Axis]
  Refine = true
  Suppressed = false
  Type = 0
FEATURE [Sketcher::SketchObject] Sketch014
  ArcFitTolerance = 1e-06
  AttachmentSupport = -> [Pocket008]
  ExternalGeometry = -> [Pocket008]
  FullyConstrained = true
  MakeInternals = false
  MapMode = 5
  Placement = pos=(0,0,14.5) rot=(0,0,1;0rad)
  sketch-geometry (8):
    g0: ArcOfCircle CenterX=30.66 CenterY=-12.875 CenterZ=0 NormalX=0 NormalY=0 NormalZ=1 AngleXU=0 Radius=5 StartAngle=4.97001 EndAngle=7.59637
    g1: ArcOfCircle CenterX=27.53 CenterY=-24.135 CenterZ=0 NormalX=0 NormalY=0 NormalZ=1 AngleXU=0 Radius=5 StartAngle=3.39921 EndAngle=6.02557
    g2: LineSegment StartX=31.9339 StartY=-8.04 StartZ=0 EndX=31.9339 EndY=-17.71 EndZ=0
    g3: LineSegment StartX=22.695 StartY=-25.4089 StartZ=0 EndX=32.365 EndY=-25.4089 EndZ=0
    g4: LineSegment StartX=-3.54 StartY=24.275 StartZ=0 EndX=1.46 EndY=24.275 EndZ=0
    g5: LineSegment StartX=1.46 StartY=24.275 StartZ=0 EndX=1.46 EndY=33.275 EndZ=0
    g6: LineSegment StartX=1.46 StartY=33.275 StartZ=0 EndX=-3.54 EndY=33.275 EndZ=0
    g7: LineSegment StartX=-3.54 StartY=33.275 StartZ=0 EndX=-3.54 EndY=24.275 EndZ=0
  constraints (23):
    c: Radius(g0) = 5
    c: Equal(g0,g1)
    c: Vertical(g2)
    c: Horizontal(g3)
    c: Coincident(g0,g2)
    c: Coincident(g2,g0)
    c: Coincident(g1,g3)
    c: Coincident(g3,g1)
    c: DistanceX(g3,g3) = 9.67
    c: DistanceY(g2,g2) = 9.67
    c: Coincident(g1,g-4)
    c: Coincident(g0,g-3)
    c: Coincident(g4,g5)
    c: Coincident(g5,g6)
    c: Coincident(g6,g7)
    c: Coincident(g7,g4)
    c: Horizontal(g4)
    c: Horizontal(g6)
    c: Vertical(g5)
    c: Vertical(g7)
    c: DistanceX(g6,g6) = 5
    c: DistanceY(g7,g7) = 9
    c: Coincident(g4,g-5)
FEATURE [PartDesign::Pad] Pad005
  BaseFeature = -> Pocket008
  Direction = (0,0,1)
  Length = 1.56
  Length2 = 10
  Profile = -> Sketch014
  ReferenceAxis = -> Sketch014 [N_Axis]
  Refine = true
  Suppressed = false
  Type = 0
FEATURE [Sketcher::SketchObject] Sketch015
  ArcFitTolerance = 1e-06
  AttachmentSupport = -> [Pad005]
  ExternalGeometry = -> [Pad005]
  FullyConstrained = true
  MakeInternals = false
  MapMode = 5
  Placement = pos=(0,0,16.06) rot=(0,0,1;0rad)
  sketch-geometry (4):
    g0: LineSegment StartX=-3.54 StartY=24.275 StartZ=0 EndX=4.46 EndY=24.275 EndZ=0
    g1: LineSegment StartX=4.46 StartY=24.275 StartZ=0 EndX=4.46 EndY=33.275 EndZ=0
    g2: LineSegment StartX=4.46 StartY=33.275 StartZ=0 EndX=-3.54 EndY=33.275 EndZ=0
    g3: LineSegment StartX=-3.54 StartY=33.275 StartZ=0 EndX=-3.54 EndY=24.275 EndZ=0
  constraints (11):
    c: Coincident(g0,g1)
    c: Coincident(g1,g2)
    c: Coincident(g2,g3)
    c: Coincident(g3,g0)
    c: Horizontal(g0)
    c: Horizontal(g2)
    c: Vertical(g1)
    c: Vertical(g3)
    c: DistanceY(g3,g3) = 9
    c: DistanceX(g2,g2) = 8
    c: Coincident(g0,g-3)
FEATURE [PartDesign::Pad] Pad006
  BaseFeature = -> Pad005
  Direction = (0,0,1)
  Length = 8.04
  Length2 = 10
  Profile = -> Sketch015
  ReferenceAxis = -> Sketch015 [N_Axis]
  Refine = true
  Suppressed = false
  Type = 0
FEATURE [Sketcher::SketchObject] Sketch016
  ArcFitTolerance = 1e-06
  AttachmentSupport = -> [Pad006]
  ExternalGeometry = -> [Pad006]
  FullyConstrained = true
  MakeInternals = false
  MapMode = 5
  Placement = pos=(0,33.275,0) rot=(1,0,0;1.5708rad)
  sketch-geometry (4):
    g0: LineSegment StartX=1.43 StartY=14.5 StartZ=0 EndX=29.43 EndY=14.5 EndZ=0
    g1: LineSegment StartX=29.43 StartY=14.5 StartZ=0 EndX=29.43 EndY=16.06 EndZ=0
    g2: LineSegment StartX=29.43 StartY=16.06 StartZ=0 EndX=1.43 EndY=16.06 EndZ=0
    g3: LineSegment StartX=1.43 StartY=16.06 StartZ=0 EndX=1.43 EndY=14.5 EndZ=0
  constraints (12):
    c: Coincident(g0,g1)
    c: Coincident(g1,g2)
    c: Coincident(g2,g3)
    c: Coincident(g3,g0)
    c: Horizontal(g0)
    c: Horizontal(g2)
    c: Vertical(g1)
    c: Vertical(g3)
    c: DistanceX(g2,g2) = 28
    c: DistanceY(g3,g3) = 1.56
    c: DistanceX(g1,g-3) = 34.83
    c: DistanceY(g1,g-3) = 8.04
FEATURE [PartDesign::Pocket] Pocket009
  BaseFeature = -> Pad006
  Direction = (0,1,-2e-16)
  Length = 1
  Length2 = 5
  Profile = -> Sketch016
  ReferenceAxis = -> Sketch016 [N_Axis]
  Refine = true
  Suppressed = false
  Type = 0
FEATURE [Sketcher::SketchObject] Sketch018
  ArcFitTolerance = 1e-06
  AttachmentSupport = -> [Pocket009]
  ExternalGeometry = -> [Pocket009]
  FullyConstrained = true
  MakeInternals = false
  MapMode = 5
  Placement = pos=(0,36.275,0) rot=(0,0.707107,0.707107;3.14159rad)
  sketch-geometry (16):
    g0: ArcOfCircle CenterX=-23.63 CenterY=17.4 CenterZ=0 NormalX=0 NormalY=0 NormalZ=1 AngleXU=0 Radius=3.75 StartAngle=1.5708 EndAngle=4.71239
    g1: ArcOfCircle CenterX=-7.23 CenterY=17.4 CenterZ=0 NormalX=0 NormalY=0 NormalZ=1 AngleXU=0 Radius=3.75 StartAngle=4.71239 EndAngle=7.85398
    g2: LineSegment StartX=-23.63 StartY=21.15 StartZ=0 EndX=-7.23 EndY=21.15 EndZ=0
    g3: LineSegment StartX=-23.63 StartY=13.65 StartZ=0 EndX=-7.23 EndY=13.65 EndZ=0
    g4: LineSegment StartX=-56.38 StartY=9.9 StartZ=0 EndX=-43.28 EndY=9.9 EndZ=0
    g5: LineSegment StartX=-43.28 StartY=9.9 StartZ=0 EndX=-43.28 EndY=24.1 EndZ=0
    g6: LineSegment StartX=-43.28 StartY=24.1 StartZ=0 EndX=-56.38 EndY=24.1 EndZ=0
    g7: LineSegment StartX=-56.38 StartY=24.1 StartZ=0 EndX=-56.38 EndY=9.9 EndZ=0
    g8: LineSegment StartX=12.42 StartY=9.9 StartZ=0 EndX=25.52 EndY=9.9 EndZ=0
    g9: LineSegment StartX=25.52 StartY=9.9 StartZ=0 EndX=25.52 EndY=24.1 EndZ=0
    g10: LineSegment StartX=25.52 StartY=24.1 StartZ=0 EndX=12.42 EndY=24.1 EndZ=0
    g11: LineSegment StartX=12.42 StartY=24.1 StartZ=0 EndX=12.42 EndY=9.9 EndZ=0
    g12: LineSegment StartX=43.28 StartY=9.9 StartZ=0 EndX=56.38 EndY=9.9 EndZ=0
    g13: LineSegment StartX=56.38 StartY=9.9 StartZ=0 EndX=56.38 EndY=24.1 EndZ=0
    g14: LineSegment StartX=56.38 StartY=24.1 StartZ=0 EndX=43.28 EndY=24.1 EndZ=0
    g15: LineSegment StartX=43.28 StartY=24.1 StartZ=0 EndX=43.28 EndY=9.9 EndZ=0
  constraints (46):
    c: Tangent(g0,g2) = 1.5708
    c: Tangent(g0,g3) = -1.5708
    c: Tangent(g1,g2) = 1.5708
    c: Tangent(g1,g3) = -1.5708
    c: Equal(g0,g1)
    c: Horizontal(g2)
    c: Radius(g0) = 3.75
    c: DistanceX(g0,g1) = 16.4
    c: DistanceX(g-3,g0) = 40.63
    c: DistanceY(g-3,g0) = 17.4
    c: Coincident(g4,g5)
    c: Coincident(g5,g6)
    c: Coincident(g6,g7)
    c: Coincident(g7,g4)
    c: Horizontal(g4)
    c: Horizontal(g6)
    c: Vertical(g5)
    c: Vertical(g7)
    c: Coincident(g8,g9)
    c: Coincident(g9,g10)
    c: Coincident(g10,g11)
    c: Coincident(g11,g8)
    c: Horizontal(g8)
    c: Horizontal(g10)
    c: Vertical(g9)
    c: Vertical(g11)
    c: Coincident(g12,g13)
    c: Coincident(g13,g14)
    c: Coincident(g14,g15)
    c: Coincident(g15,g12)
    c: Horizontal(g12)
    c: Horizontal(g14)
    c: Vertical(g13)
    c: Vertical(g15)
    c: DistanceX(g4,g4) = 13.1
    c: Equal(g4,g8)
    c: Equal(g12,g8)
    c: Equal(g15,g9)
    c: Equal(g11,g5)
    c: DistanceY(g6,g-3) = 0
    c: DistanceY(g10,g5) = 0
    c: DistanceY(g14,g9) = 0
    c: DistanceX(g-3,g4) = 7.88
    c: DistanceX(g12,g-4) = 7.88
    c: DistanceX(g8,g12) = 17.76
    c: DistanceY(g11,g11) = 14.2
FEATURE [PartDesign::CoordinateSystem] Local_CS
  AttacherType = Attacher::AttachEngine3D
  MapMode = 2
FEATURE [PartDesign::Pocket] Pocket010
  BaseFeature = -> Pocket009
  Direction = (0,-1,2e-16)
  Length = 3
  Length2 = 5
  Profile = -> Sketch018
  ReferenceAxis = -> Sketch018 [N_Axis]
  Refine = true
  Suppressed = false
  Type = 0
FEATURE [Sketcher::SketchObject] Sketch017
  ArcFitTolerance = 1e-06
  AttachmentSupport = -> [Pocket009]
  FullyConstrained = true
  MakeInternals = false
  MapMode = 5
  Placement = pos=(0,0,3) rot=(0,0,1;0rad)
FEATURE [PartDesign::Body] Body
  AllowCompound = false
  Group = -> [Sketch,Pad,Sketch001,Pocket,Sketch002,Pad001,Sketch003,Pocket001,Sketch004,Pad002,Sketch005,Pocket002,Sketch006,Pad003,Sketch007,Pocket003,Sketch008,Pad004,Sketch009,Pocket004,Sketch010,Pocket005,Sketch011,Pocket006,Sketch012,Pocket007,Sketch013,Pocket008,Sketch014,Pad005,Sketch015,Pad006,Sketch016,Pocket009,Sketch017,Sketch018,Pocket010,Local_CS]
  Origin = -> Origin
  Tip = -> Pocket010
